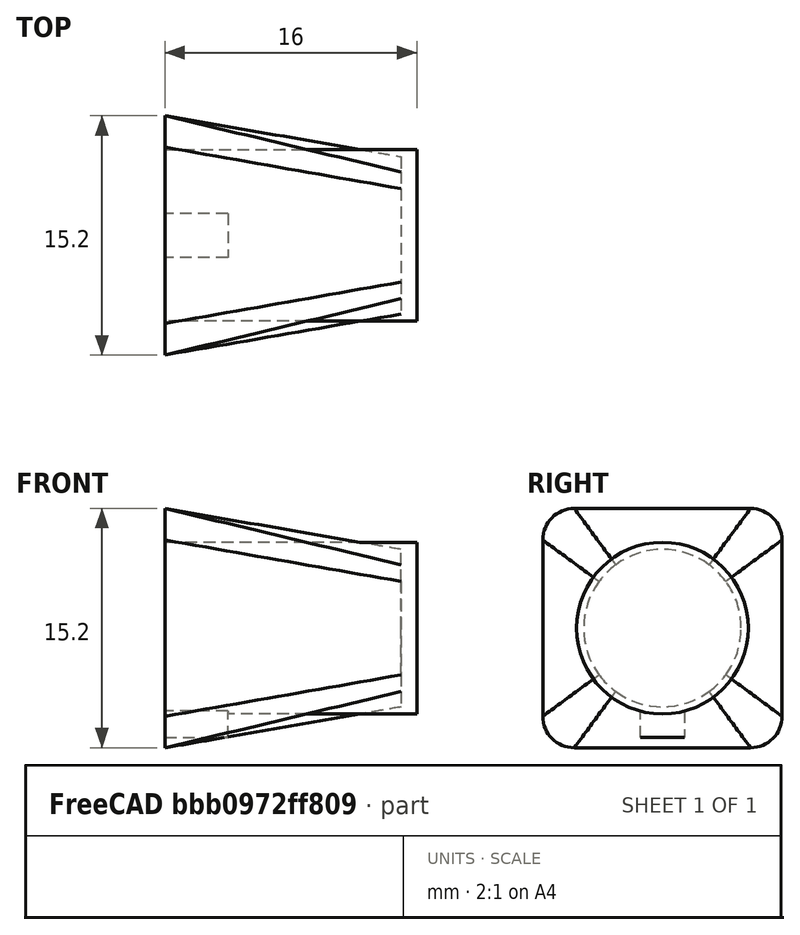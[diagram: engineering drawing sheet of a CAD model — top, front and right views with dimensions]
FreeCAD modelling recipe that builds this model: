
FCSTD DOCUMENT  (FreeCAD 1.0R39109 (Git))
Label: abu-mount
License: All rights reserved
LicenseURL: http://en.wikipedia.org/wiki/All_rights_reserved
objects: Sketcher::SketchObject×4, PartDesign::Pad×2, PartDesign::Body×2, App::Link×2, App::FeaturePython×2, PartDesign::AdditiveLoft×1, Assembly::JointGroup×1, Assembly::AssemblyObject×1
note: 19 computed .brp shape members not serialized (recipe doc carries the construction recipe); baked Part::Feature solids carry a one-line shape summary decoded from their .brp

FEATURE [Sketcher::SketchObject] Sketch002  label="Start001"
  ArcFitTolerance = 1e-06
  FullyConstrained = true
  MakeInternals = false
  MapMode = 5
  Placement = pos=(0,0,0) rot=(0.57735,0.57735,0.57735;2.0944rad)
  sketch-geometry (8):
    g0: LineSegment StartX=-7.6 StartY=-5.6 StartZ=0 EndX=-7.6 EndY=5.6 EndZ=0
    g1: ArcOfCircle CenterX=-5.6 CenterY=5.6 CenterZ=0 NormalX=0 NormalY=0 NormalZ=1 AngleXU=0 Radius=2 StartAngle=1.5708 EndAngle=3.14159
    g2: LineSegment StartX=-5.6 StartY=7.6 StartZ=0 EndX=5.6 EndY=7.6 EndZ=0
    g3: ArcOfCircle CenterX=5.6 CenterY=5.6 CenterZ=0 NormalX=0 NormalY=0 NormalZ=1 AngleXU=0 Radius=2 StartAngle=2e-16 EndAngle=1.5708
    g4: LineSegment StartX=7.6 StartY=5.6 StartZ=0 EndX=7.6 EndY=-5.6 EndZ=0
    g5: ArcOfCircle CenterX=5.6 CenterY=-5.6 CenterZ=0 NormalX=0 NormalY=0 NormalZ=1 AngleXU=0 Radius=2 StartAngle=4.71239 EndAngle=6.28319
    g6: LineSegment StartX=5.6 StartY=-7.6 StartZ=0 EndX=-5.6 EndY=-7.6 EndZ=0
    g7: ArcOfCircle CenterX=-5.6 CenterY=-5.6 CenterZ=0 NormalX=0 NormalY=0 NormalZ=1 AngleXU=0 Radius=2 StartAngle=3.14159 EndAngle=4.71239
  constraints (19):
    c: Vertical(g0)
    c: Tangent(g0,g1) = 1.5708
    c: Tangent(g1,g2) = 1.5708
    c: Tangent(g2,g3) = 1.5708
    c: Tangent(g3,g4) = 1.5708
    c: Tangent(g4,g5) = 1.5708
    c: Tangent(g5,g6) = 1.5708
    c: Parallel(g2,g-1)
    c: Parallel(g6,g-1)
    c: Parallel(g4,g-2)
    c: Equal(g2,g4)
    c: Equal(g4,g6)
    c: Equal(g6,g0)
    c: Equal(g1,g3)
    c: Tangent(g7,g6) = 1.5708
    c: Tangent(g7,g0) = 1.5708
    c: Radius(g1) = 2
    c: DistanceX(g0,g3) = 15.2
    c: Symmetric(g3,g7,g-1)
FEATURE [Sketcher::SketchObject] Sketch005  label="End001"
  ArcFitTolerance = 1e-06
  FullyConstrained = true
  MakeInternals = false
  MapMode = 5
  Placement = pos=(15,0,0) rot=(0.57735,0.57735,0.57735;2.0944rad)
  sketch-geometry (1):
    g0: Circle CenterX=0 CenterY=0 CenterZ=0 NormalX=0 NormalY=0 NormalZ=1 AngleXU=0 Radius=5
  constraints (2):
    c: Coincident(g0,g-1)
    c: Diameter(g0) = 10
FEATURE [Sketcher::SketchObject] Sketch006  label="Cylinder"
  ArcFitTolerance = 1e-06
  AttachmentSupport = -> [YZ_Plane004]
  FullyConstrained = true
  MakeInternals = false
  MapMode = 5
  Placement = pos=(0,0,0) rot=(0.57735,0.57735,0.57735;2.0944rad)
  sketch-geometry (1):
    g0: Circle CenterX=0 CenterY=0 CenterZ=0 NormalX=0 NormalY=0 NormalZ=1 AngleXU=0 Radius=5.45
  constraints (2):
    c: Coincident(g0,g-1)
    c: Diameter(g0) = 10.9
FEATURE [PartDesign::Pad] Pad001
  Direction = (1,0,0)
  Length = 16
  Length2 = 10
  Placement = pos=(0,0,0) rot=(1,1,1;2.0944rad)
  Profile = -> Sketch006
  ReferenceAxis = -> Sketch006 [N_Axis]
  Refine = true
  Suppressed = false
  Type = 0
FEATURE [Sketcher::SketchObject] Sketch007
  ArcFitTolerance = 1e-06
  AttachmentSupport = -> [YZ_Plane004]
  FullyConstrained = true
  MakeInternals = false
  MapMode = 5
  Placement = pos=(0,0,0) rot=(0.57735,0.57735,0.57735;2.0944rad)
  sketch-geometry (5):
    g0: LineSegment StartX=-1.4 StartY=0 StartZ=0 EndX=1.4 EndY=0 EndZ=0
    g1: LineSegment StartX=1.4 StartY=0 StartZ=0 EndX=1.4 EndY=-6.95 EndZ=0
    g2: LineSegment StartX=1.4 StartY=-6.95 StartZ=0 EndX=-1.4 EndY=-6.95 EndZ=0
    g3: LineSegment StartX=-1.4 StartY=-6.95 StartZ=0 EndX=-1.4 EndY=0 EndZ=0
    g4: LineSegment [constr] StartX=0 StartY=0 StartZ=0 EndX=0 EndY=-5.45 EndZ=0
  constraints (13):
    c: Coincident(g0,g1)
    c: Coincident(g1,g2)
    c: Coincident(g2,g3)
    c: Coincident(g3,g0)
    c: Horizontal(g0)
    c: Vertical(g1)
    c: DistanceX(g2,g2) = 2.8
    c: Symmetric(g2,g1,g-2)
    c: Coincident(g4,g-1)
    c: PointOnObject(g4,g-2)
    c: DistanceY(g4,g4) = 5.45
    c: DistanceY(g1,g4) = 1.5
    c: Symmetric(g0,g0,g4)
FEATURE [PartDesign::Pad] Pad002  label="Rotation Lock"
  BaseFeature = -> Pad001
  Direction = (1,0,0)
  Length = 4
  Length2 = 10
  Placement = pos=(0,0,0) rot=(1,1,1;2.0944rad)
  Profile = -> Sketch007
  ReferenceAxis = -> Sketch007 [N_Axis]
  Refine = true
  Suppressed = false
  Type = 0
FEATURE [PartDesign::Body] Body003  label="Shaft"
  AllowCompound = false
  Group = -> [Sketch006,Pad001,Sketch007,Pad002]
  Origin = -> Origin004
  Tip = -> Pad002
FEATURE [App::Link] Shaft  label="Shaft001"
  LinkPlacement = pos=(4.95325e-10,3e-16,-20.3005) rot=(3e-06,0,1;0rad)
  LinkedObject = -> Body003
  Placement = pos=(4.95325e-10,3e-16,-20.3005) rot=(3e-06,0,1;0rad)
FEATURE [App::Link] Connector  label="Connector001"
  LinkPlacement = pos=(4.95325e-10,1.3e-15,-20.5764) rot=(0,1,0;3.14159rad)
  LinkedObject = -> Body002
  Placement = pos=(4.95325e-10,1.3e-15,-20.5764) rot=(0,1,0;3.14159rad)
FEATURE [PartDesign::AdditiveLoft] AdditiveLoft
  Closed = false
  Placement = pos=(0,0,0) rot=(0.57735,0.57735,0.57735;2.0944rad)
  Profile = -> Sketch002
  Refine = true
  Ruled = false
  Sections = -> [Sketch005]
  Suppressed = false
FEATURE [PartDesign::Body] Body002  label="Connector"
  AllowCompound = false
  Group = -> [Sketch002,Sketch005,AdditiveLoft]
  Origin = -> Origin003
  Tip = -> AdditiveLoft
FEATURE [App::FeaturePython] GroundedJoint  # Assembly grounded joint (typed FeaturePython)
  ObjectToGround = -> Shaft
  Placement = pos=(4.95325e-10,3e-16,-20.3005) rot=(2e-06,0,0.904095;0rad)
FEATURE [App::FeaturePython] Joint  label="Fixed"  # Assembly joint (typed FeaturePython)
  Activated = true
  AngleMax = 0
  AngleMin = 0
  Detach1 = false
  Detach2 = false
  Distance = 0
  Distance2 = 0
  EnableAngleMax = false
  EnableAngleMin = false
  EnableLengthMax = false
  EnableLengthMin = false
  JointType = 0 (Fixed)
  LengthMax = 0
  LengthMin = 0
  Offset2 = pos=(0,0,0) rot=(0,0,1;1.5708rad)
  Placement1 = pos=(-1e-16,-1.97e-14,-0.275941) rot=(0.707107,0,-0.707107;3.14159rad)
  Placement2 = pos=(0,6e-16,0) rot=(0.707107,0,0.707107;3.14159rad)
  Reference1 = -> Assembly [Shaft.Face7,Shaft.Face7]
  Reference2 = -> Assembly [Connector.Face1,Connector.Face1]
FEATURE [Assembly::JointGroup] Joints
  Group = -> [GroundedJoint,Joint]
FEATURE [Assembly::AssemblyObject] Assembly
  Group = -> [Joints,Shaft,Connector,GroundedJoint,Joint]
  Origin = -> Origin
  Type = Assembly
